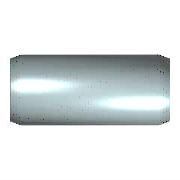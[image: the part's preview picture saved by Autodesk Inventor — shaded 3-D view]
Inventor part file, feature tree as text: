
AUTODESK INVENTOR PART (.ipt)
format: ipt  version: 2023.3 (Build 273359000, 359)  size: 117,248 bytes
history: native  units: mm (DEFAULTED — no unit token found)
features: extrude x1, chamfer x1, sketch x1
ambient origin geometry x8: Origin, YZ Plane, XZ Plane, XY Plane, X Axis, Y Axis, Z Axis, Center Point
bodies: Solid1 (feature_tree)
feature tree (3):
  extrude  "Körper"  Depth=8.0mm
  chamfer  "Skizze2"  [1 undecoded]
  sketch  "Skizze"  dims[d1=3.0mm d2=8.0mm d3=0.0mm d4=0.5mm d5=15.0deg d8=0.5mm d9=15.0deg d11=0.5mm d12=0.5mm d13=0.0mm d15=0.0mm d16=0.0mm]
note: 1 required parameter value undecoded (feature->parameter linkage not recoverable at this tier; creation-order binding heuristic only, values carry confidence <= 0.55)
